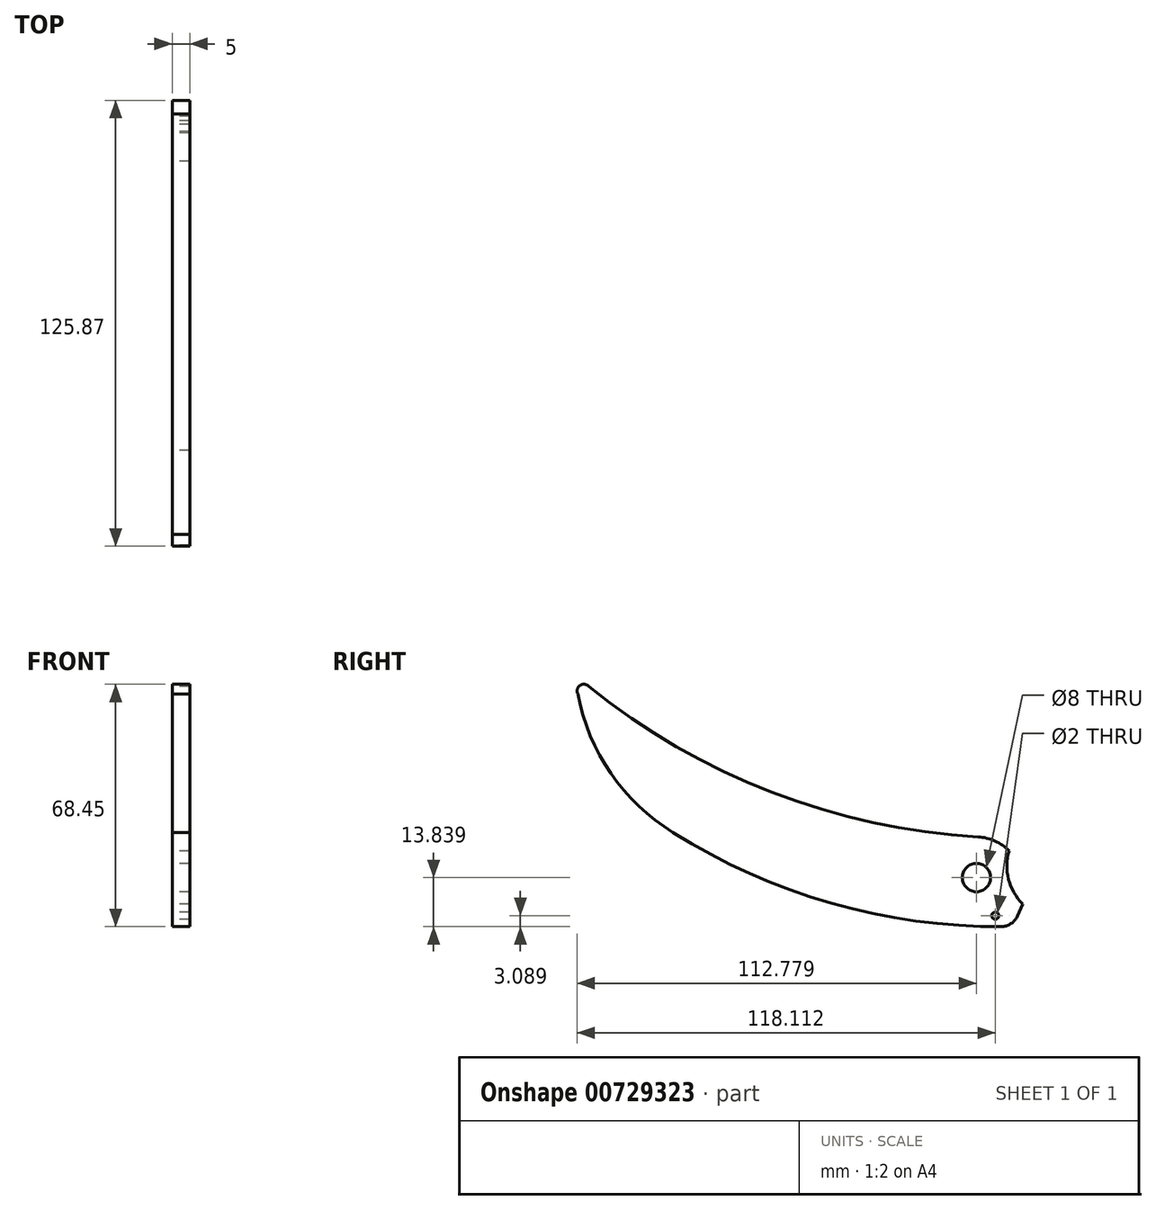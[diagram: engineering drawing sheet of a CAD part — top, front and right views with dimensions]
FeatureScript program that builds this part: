
annotation { "Feature Type Name" : "Feature", "Feature Type Description" : "" }
export const myFeature = defineFeature(function(context is Context, id is Id, definition is map)
    precondition{}
    {
        {
            var Q0;
            Q0=qCreatedBy(makeId("Right.planeOp"),FACE);
            var sketch = newSketch(context, id + "F0", { "sketchPlane" : qUnion([Q0])});
            skLineSegment(sketch, "E0", {"start": v(50.96, -23.71) * mm, "end": v(49.4, -27.18) * mm});
            skCircle(sketch, "E1", {"center": v(37.87, -16.26) * mm, "radius": 4 * mm});
            skCircle(sketch, "E2.0", {"center": v(37.87, -16.26) * mm, "radius": 12 * mm, "construction": true});
            skLineSegment(sketch, "E3.0", {"start": v(35.34, -20.49) * mm, "end": v(44.53, -28.11) * mm, "construction": true});
            skCircle(sketch, "E4", {"center": v(43.2, -27.01) * mm, "radius": 1 * mm});
            skPoint(sketch, "E5.visualSharp", {"position": v(47.7, -30.94) * mm});
            skArc(sketch, "E5.filletArc", {"start": v(45.24, -30.1) * mm, "mid": v(47.72, -29.2) * mm, "end": v(49.4, -27.18) * mm});
            skPoint(sketch, "E6.visualSharp", {"position": v(55.93, -12.72) * mm});
            skLineSegment(sketch, "E7", {"start": v(37.87, -16.26) * mm, "end": v(34.03, -24.76) * mm, "construction": true});
            skArc(sketch, "E8", {"start": v(47.09, -8.72) * mm, "mid": v(46.94, -16.75) * mm, "end": v(50.96, -23.71) * mm});
            skArc(sketch, "E9", {"start": v(-71.65, 37.75) * mm, "mid": v(-19.98, 7.86) * mm, "end": v(38.36, -4.77) * mm});
            skArc(sketch, "E10", {"start": v(-47.83, -3.48) * mm, "mid": v(-3.2, -23.49) * mm, "end": v(45.24, -30.1) * mm});
            skArc(sketch, "E11", {"start": v(-71.65, 37.75) * mm, "mid": v(-74.14, 38) * mm, "end": v(-74.67, 35.55) * mm});
            skArc(sketch, "E12", {"start": v(-74.67, 35.55) * mm, "mid": v(-65.38, 13.19) * mm, "end": v(-47.83, -3.48) * mm});
            skArc(sketch, "E13", {"start": v(38.36, -4.77) * mm, "mid": v(43.09, -5.93) * mm, "end": v(47.09, -8.72) * mm});
            skSolve(sketch);
        }
        {
            var Q0;
            Q0 = qSketchRegion(id + "F0", true);
            extrude(context, id + "F1", {"entities" : qUnion([Q0]), "depth" : 5 * mm, "offsetDistance" : 25 * mm});
        }
    });
